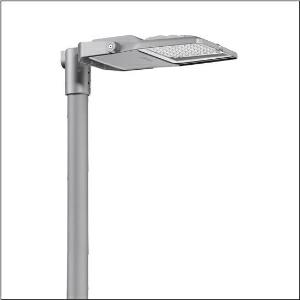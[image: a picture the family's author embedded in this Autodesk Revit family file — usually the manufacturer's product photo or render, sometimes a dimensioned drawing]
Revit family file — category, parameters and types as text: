
# Revit family: floodlight_fl_21_mini___pl33t_5xa7776c2f3a_ca81
name_source: partatom
category: Lighting Fixtures
units: mm (PartAtom-declared; Revit-internal decimal feet)

## family parameters
Cut with Voids When Loaded = No
Host = Face
Light Source = No
Part Type = Normal
Room Calculation Point = No
Round Connector Dimension = Use Diameter
Shared = No

## types (1)
- --- (1 x LED, 12050 lm, 89 W, 3000K)
    Apparent Load = 89 VA
    CIE Flux Codes = 26 75 99 100 100
    Color Rendering = 70
    Color Temperature = 3000K
    Default Elevation = 1800 mm
    Description = Floodlight FL 21 mini, floodlight, primary light control with lens, of PMMA, primary optical cover: protective disc, of toughened safety glass, transparent, light distribution: PL33T, light emission: direct distribution, installation type: surface-mounted, LED, High Power LED, rated luminous flux: 12.050lm, luminous efficacy: 135lm/W, light colour: 730, colour temperature: 3000K, control: flexible luminous flux parameterisation, time-dependent luminous flux control, constant luminous flux control, overheat protection, presetting dimming logarithmic, with terminal, 6-pole, mains connection: 220..240V, AC, 50/60Hz, start of lifetime: 89W, end of service life: 94W, reduction: 43W, luminaire housing, of diecast aluminium, powder-coated, Siteco® metallic grey (DB 702S), corrosivity category C5 mid according to DIN EN ISO 12944, sealing non-destructively replaceable, please order mast flange separately, mast bracket, of steel, galvanised, powder-coated, Siteco® metallic grey (DB 702S), Smart Interface below and above, protection rating (complete): IP66, insulation class (complete): insulation class II (safety insulation), certification: CE, ENEC, VDE, protection symbol: D, impact resistance: IK08, permissible operating ambient temperature: -40..+40°C, permissible operating ambient temperature for outdoor applications: -40..+50°C, standard: DIN EN 12944, LABS conformity tested according to VDMA 24364:2018-05, packaging unit: 1 piece

Light Distribution: PL33T
    Height = 70 mm
    Lamp = 1 x LED
    Lamp Light Flux = 12050 lm
    Lamp Power = 89 W
    Lamp count = 1
    Length = 485 mm
    Luminous efficacy = 135 lm/W
    Manufacturer = Siteco
    ModVariant = No
    Model = 5XA7776C2F3A
    Number of Poles = 1
    OnlyDefault = Yes
    Power Factor = 1
    Product Name = Floodlight FL 21 mini | PL33T
    Product group = floodlight | pylon annexe
    ProductGroupID = 6200
    Protection Class = Protection class II
    Protection Degree = IP 66
    RLX_Detail_Level = 1
    RLX_Emergency_Light_Flux = 0 lm
    RLX_Emergency_Type = 0
    RLX_Emergency_Type_DB = No
    RlxData = <blob elided: 100677 chars, md5=b6b5f640>
    Socket = socket
    Standby Power = 0 W
    System Light Flux = 12050 lm
    System Power = 89 W
    Type Comments = factory setting: luminous flux: 100 % | dim-lin: 254 | 456 mA
    Type Image = l_1007125.jpg
    URL = http://relux.com
    VarID = @adj_080961
    Voltage = 0 V
    Weight = 0.00 kg
    Width = 337 mm

## geometry (parser evidence)
native form markers: Blend x4, Sweep x11
no freeform markers — native parametric forms only
